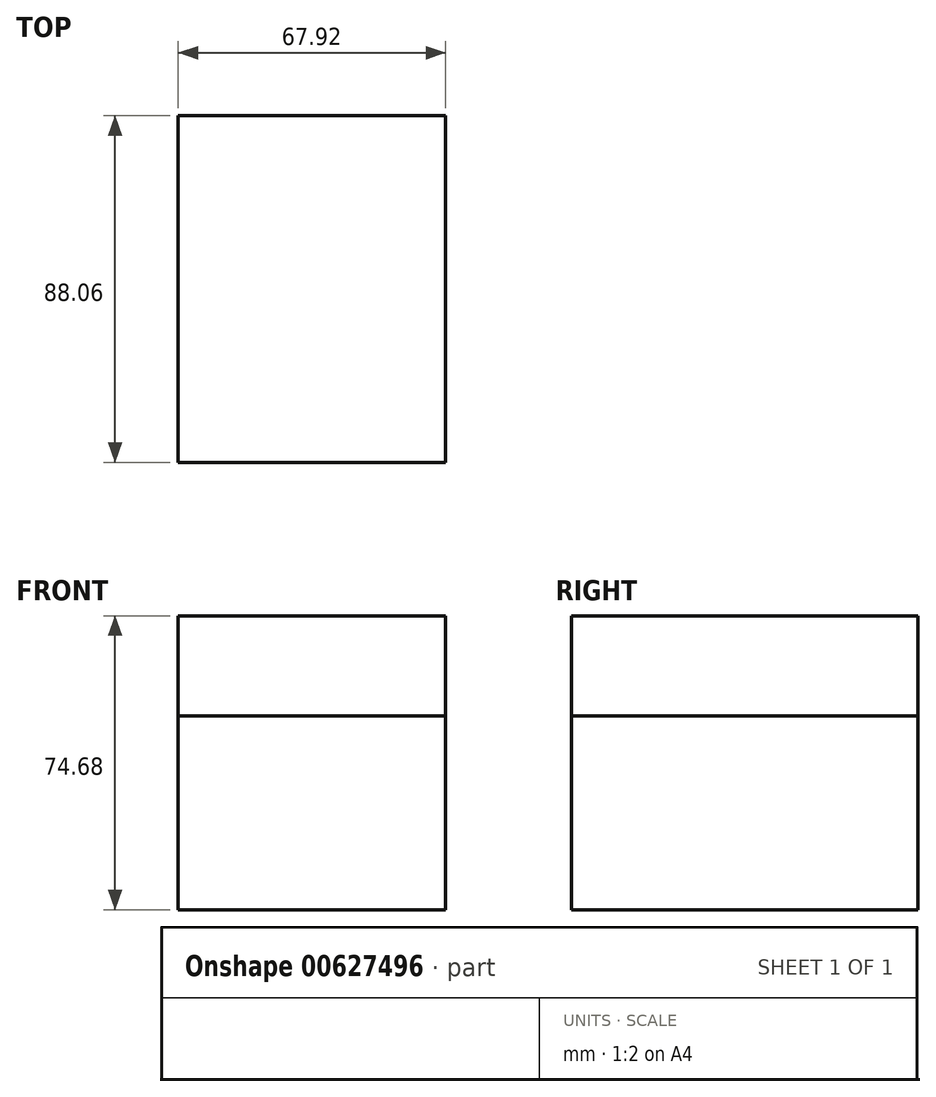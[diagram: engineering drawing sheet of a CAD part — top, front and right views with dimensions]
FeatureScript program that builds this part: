
annotation { "Feature Type Name" : "Feature", "Feature Type Description" : "" }
export const myFeature = defineFeature(function(context is Context, id is Id, definition is map)
    precondition{}
    {
        {
            var Q0;
            Q0=qCreatedBy(makeId("Top.planeOp"),FACE);
            var sketch = newSketch(context, id + "F0", { "sketchPlane" : qUnion([Q0])});
            skLineSegment(sketch, "E0.bottom", {"start": v(33.96, 44.03) * mm, "end": v(-33.96, 44.03) * mm});
            skLineSegment(sketch, "E0.top", {"start": v(33.96, -44.03) * mm, "end": v(-33.96, -44.03) * mm});
            skLineSegment(sketch, "E0.left", {"start": v(33.96, 44.03) * mm, "end": v(33.96, -44.03) * mm});
            skLineSegment(sketch, "E0.right", {"start": v(-33.96, 44.03) * mm, "end": v(-33.96, -44.03) * mm});
            skPoint(sketch, "E0.middle", {"position": v(0, 0) * mm});
            skSolve(sketch);
        }
        {
            var Q0;
            Q0=makeQuery(id+"F0.imprint","IMPRINT",FACE,{"disambiguationData":[TD([[makeQuery(id+"F0.imprint","IMPRINT",EDGE,{"derivedFrom":sQuery(id+"F0.wireOp",EDGE,"E0.bottom")}),1.0]])]});
            extrude(context, id + "F1", {"entities" : qUnion([Q0]), "oppositeDirection" : true, "depth" : 49.28 * mm, "offsetDistance" : 25.4 * mm});
        }
        {
            var Q0;
            Q0=makeQuery(id+"F0.imprint","IMPRINT",FACE,{"disambiguationData":[TD([[makeQuery(id+"F0.imprint","IMPRINT",EDGE,{"derivedFrom":sQuery(id+"F0.wireOp",EDGE,"E0.bottom")}),1.0]])]});
            extrude(context, id + "F2", {"entities" : qUnion([Q0]), "depth" : 25.4 * mm});
        }
    });
